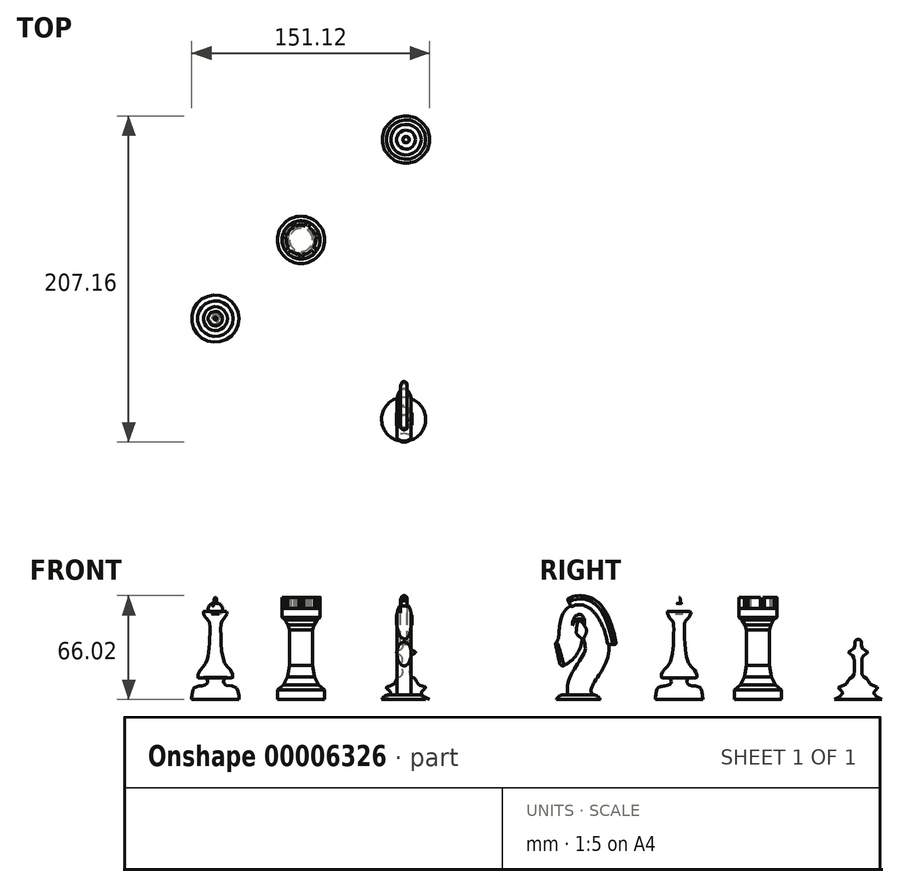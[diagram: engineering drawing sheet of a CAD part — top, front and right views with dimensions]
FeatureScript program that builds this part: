
annotation { "Feature Type Name" : "Feature", "Feature Type Description" : "" }
export const myFeature = defineFeature(function(context is Context, id is Id, definition is map)
    precondition{}
    {
        {
            var Q0;
            Q0=qCreatedBy(makeId("Front.planeOp"),FACE);
            var sketch = newSketch(context, id + "F0", { "sketchPlane" : qUnion([Q0])});
            skLineSegment(sketch, "E0", {"start": v(-54.42, 8.51) * mm, "end": v(-39.42, 8.51) * mm});
            skLineSegment(sketch, "E1", {"start": v(-54.42, 8.51) * mm, "end": v(-54.42, 73.51) * mm});
            skPoint(sketch, "E2.1.internal.orphan", {"position": v(-39.42, 9.76) * mm});
            skPoint(sketch, "E3.1.internal.orphan", {"position": v(-52.69, 73.51) * mm});
            skFitSpline(sketch, "E4", {"points": [v(-54.42, 73.51) * mm, v(-53.55, 72.1) * mm, v(-53.46, 69.73) * mm, v(-52.69, 69.64) * mm, v(-50.55, 68.18) * mm, v(-50.2, 65.25) * mm, v(-52.02, 62.88) * mm, v(-47.1, 64.52) * mm, v(-48.6, 60.17) * mm, v(-50.48, 58.23) * mm, v(-50.97, 52.34) * mm, v(-50.18, 38.13) * mm, v(-47.52, 30.23) * mm, v(-44.3, 26.7) * mm, v(-43.47, 22.32) * mm, v(-47.93, 22.35) * mm, v(-49, 18.48) * mm, v(-41.7, 16.43) * mm, v(-39.8, 12.66) * mm, v(-39.42, 8.51) * mm], "startDerivative": vector(29.5, -28.55) * mm, "endDerivative": vector(-7.12, -67.96) * mm});
            skSolve(sketch);
        }
        {
            var Q0;
            Q0=makeQuery(id+"F0.imprint","IMPRINT",FACE,{"disambiguationData":[TD([[makeQuery(id+"F0.imprint","IMPRINT",EDGE,{"derivedFrom":sQuery(id+"F0.wireOp",EDGE,"E0")}),1.0]])]});
            var Q1;
            Q1=sQuery(id+"F0.wireOp",EDGE,"E1");
            revolve(context, id + "F1", {"entities" : qUnion([Q0]), "axis" : qUnion([Q1]), "revolveType" : RevolveType.FULL});
        }
        {
            var Q0;
            Q0=qCreatedBy(makeId("Top.planeOp"),FACE);
            var sketch = newSketch(context, id + "F2", { "sketchPlane" : qUnion([Q0])});
            skCircle(sketch, "E5", {"center": v(65.14, -64.02) * mm, "radius": 14 * mm});
            skSolve(sketch);
        }
        {
            var Q0;
            Q0=makeQuery(id+"F2.imprint","IMPRINT",FACE,{"disambiguationData":[TD([[makeQuery(id+"F2.imprint","IMPRINT",EDGE,{"derivedFrom":sQuery(id+"F2.wireOp",EDGE,"E5")}),1.0]])]});
            extrude(context, id + "F3", {"entities" : qUnion([Q0]), "depth" : 3 * mm});
        }
        {
            var Q0;
            Q0=makeQuery(id+"F3.opExtrude","CAP_EDGE",EDGE,{"disambiguationData":[OSD([sQuery(id+"F2.wireOp",EDGE,"E5")])],"isStart":false});
            fillet(context, id + "F4", {"entities" : qUnion([Q0]), "radius" : 5 * mm, "tangentPropagation" : true, "allowEdgeOverflow" : false});
        }
        {
            var Q0;
            Q0=makeQuery(id+"F3.opExtrude","CAP_FACE",FACE,{"disambiguationData":[OSD([sQuery(id+"F2.wireOp",EDGE,"E5")])],"isStart":false});
            var sketch = newSketch(context, id + "F5", { "sketchPlane" : qUnion([Q0])});
            skLineSegment(sketch, "E6", {"start": v(65.48, -63.98) * mm, "end": v(65.48, -61.79) * mm, "construction": true});
            skPoint(sketch, "E7", {"position": v(65.48, -62.88) * mm});
            skEllipse(sketch, "E8", {"center": v(65.48, -62.88) * mm, "majorRadius": 7.78 * mm, "minorRadius": 4.5 * mm, "majorAxis": v(-0.01, 1)});
            skSolve(sketch);
        }
        {
            var Q0;
            Q0=sQuery(id+"F5.wireOp",EDGE,"E6");
            var Q1;
            Q1=sQuery(id+"F5.wireOp",EDGE,"7c3d4466-9b8f-44b1-8b03-aff673ece0ba.0");
            cPlane(context, id + "F6", {"entities" : qUnion([Q0, Q1]), "cplaneType" : CPlaneType.LINE_ANGLE, "offset" : 5 * mm, "angle" : 90 * degree, "width" : 150 * mm, "height" : 150 * mm});
        }
        {
            var Q0;
            Q0=qCreatedBy(id+"F6.planeOp",FACE);
            var sketch = newSketch(context, id + "F7", { "sketchPlane" : qUnion([Q0])});
            skLineSegment(sketch, "E9.0", {"start": v(-63.98, 3) * mm, "end": v(-61.79, 3) * mm});
            skPoint(sketch, "E10", {"position": v(-62.88, 3) * mm});
            skLineSegment(sketch, "E11", {"start": v(-61.79, 3) * mm, "end": v(-61.79, 53) * mm, "construction": true});
            skFitSpline(sketch, "E12", {"points": [v(-62.88, 3) * mm, v(-62.88, 9.44) * mm, v(-57.92, 18.86) * mm, v(-52.19, 33.4) * mm, v(-61.79, 53) * mm, v(-66.92, 50.95) * mm, v(-68.93, 40.26) * mm, v(-77.02, 28.25) * mm], "startDerivative": vector(-13.9, 64.01) * mm, "endDerivative": vector(-112.3, -51.14) * mm});
            skSolve(sketch);
        }
        {
            var Q0;
            Q0=makeQuery(id+"F5.imprint","IMPRINT",FACE,{"disambiguationData":[TD([[makeQuery(id+"F5.imprint","IMPRINT",EDGE,{"derivedFrom":sQuery(id+"F5.wireOp",EDGE,"E8")}),1.0]])]});
            var Q1;
            Q1=sQuery(id+"F7.wireOp",EDGE,"E12");
            sweep(context, id + "F8", {"operationType" : NewBodyOperationType.ADD, "profiles" : qUnion([Q0]), "path" : qUnion([Q1])});
        }
        {
            var Q0;
            Q0=qCreatedBy(id+"F6.planeOp",FACE);
            cPlane(context, id + "F9", {"entities" : qUnion([Q0]), "cplaneType" : CPlaneType.OFFSET, "offset" : 25 * mm, "width" : 150 * mm, "height" : 150 * mm});
        }
        {
            var Q0;
            Q0=qCreatedBy(id+"F9.planeOp",FACE);
            var sketch = newSketch(context, id + "F10", { "sketchPlane" : qUnion([Q0])});
            skFitSpline(sketch, "E13.0", {"points": [v(-62.37, 3) * mm, v(-62.85, 5.23) * mm, v(-64.4, 10.59) * mm, v(-50.33, 16.4) * mm, v(-51.17, 32.87) * mm, v(-58.28, 56.27) * mm, v(-68.89, 51.46) * mm, v(-68.1, 39.65) * mm, v(-71.15, 30.92) * mm, v(-77.02, 28.25) * mm]});
            skCircle(sketch, "E14", {"center": v(-63.7, 48.76) * mm, "radius": 10.57 * mm});
            skSolve(sketch);
        }
        {
            var Q0;
            {var subQ0=sQuery(id+"F10.wireOp",EDGE,"E14");var subQ1=sQuery(id+"F10.wireOp",EDGE,"E13.0");var subQ3=makeQuery(id+"F10.imprint","INTERSECT",VERTEX,{"disambiguationData":[OD(0.0)],"derivedFrom":[subQ1,subQ0]});Q0=makeQuery(id+"F10.imprint","IMPRINT",FACE,{"disambiguationData":[TD([[makeQuery(id+"F10.imprint","IMPRINT",EDGE,{"disambiguationData":[TD([[subQ3,1.0]])],"derivedFrom":subQ1}),-1.0]])]});}
            var Q1;
            {var subQ0=sQuery(id+"F10.wireOp",EDGE,"E14");var subQ1=sQuery(id+"F10.wireOp",EDGE,"E13.0");var subQ3=makeQuery(id+"F10.imprint","INTERSECT",VERTEX,{"disambiguationData":[OD(0.0)],"derivedFrom":[subQ1,subQ0]});Q1=makeQuery(id+"F10.imprint","IMPRINT",FACE,{"disambiguationData":[TD([[makeQuery(id+"F10.imprint","IMPRINT",EDGE,{"disambiguationData":[TD([[subQ3,1.0]])],"derivedFrom":subQ1}),1.0]])]});}
            extrude(context, id + "F11", {"entities" : qUnion([Q0, Q1]), "depth" : 8.2 * mm});
        }
        {
            var Q0;
            Q0=qCreatedBy(makeId("Top.planeOp"),FACE);
            var sketch = newSketch(context, id + "F12", { "sketchPlane" : qUnion([Q0])});
            skFitSpline(sketch, "E15.0", {"points": [v(64.78, -54.59) * mm, v(1000, 55.78) * mm, v(-54.68, 333.33) * mm, v(55.94, -70.24) * mm, v(333.33, 64.94) * mm, v(-70.15, 1000) * mm, v(73.94, -70.06) * mm, v(64.78, -54.59) * mm]});
            skLineSegment(sketch, "E16.0", {"start": v(98.68, -53.13) * mm, "end": v(98.68, -74.28) * mm});
            skLineSegment(sketch, "E17", {"start": v(98.68, -63.7) * mm, "end": v(94.58, -63.7) * mm, "construction": true});
            skPoint(sketch, "E18.orphan", {"position": v(90.48, -74.28) * mm});
            skPoint(sketch, "E19.0.start.orphan", {"position": v(90.48, -53.13) * mm});
            skPoint(sketch, "E20", {"position": v(94.58, -63.7) * mm});
            skPoint(sketch, "E21.orphan", {"position": v(90.48, -63.7) * mm});
            skLineSegment(sketch, "E22", {"start": v(61, -62.21) * mm, "end": v(65.48, -62.21) * mm, "construction": true});
            skPoint(sketch, "E23", {"position": v(65.48, -62.21) * mm});
            skPoint(sketch, "E24.orphan", {"position": v(69.96, -62.21) * mm});
            skLineSegment(sketch, "E25", {"start": v(65.48, -62.21) * mm, "end": v(94.58, -62.21) * mm});
            skLineSegment(sketch, "E26", {"start": v(65.48, -62.21) * mm, "end": v(65.48, -55.1) * mm});
            skSolve(sketch);
        }
        {
            var Q0;
            Q0=makeQuery(id+"F11.opExtrude","CAP_EDGE",EDGE,{"disambiguationData":[OSD([sQuery(id+"F10.wireOp",EDGE,"E14")])],"isStart":true});
            fillet(context, id + "F13", {"entities" : qUnion([Q0]), "radius" : 5 * mm, "tangentPropagation" : true, "allowEdgeOverflow" : false});
        }
        {
            var Q0;
            Q0=makeQuery(id+"F11.opExtrude","SWEPT_FACE",FACE,{"disambiguationData":[OSD([sQuery(id+"F10.wireOp",EDGE,"E14")])]});
            var Q1;
            Q1=makeQuery(id+"F11.opExtrude","CAP_EDGE",EDGE,{"disambiguationData":[OSD([sQuery(id+"F10.wireOp",EDGE,"E14")])],"isStart":false});
            fillet(context, id + "F14", {"entities" : qUnion([Q0, Q1]), "radius" : 5 * mm, "tangentPropagation" : true, "allowEdgeOverflow" : false});
        }
        {
            var Q0;
            Q0=makeQuery(id+"F11.opExtrude","SWEPT_BODY",BODY,{"disambiguationData":[OSD([sQuery(id+"F10.wireOp",EDGE,"E14")])]});
            var Q1;
            Q1=sQuery(id+"F12.wireOp",EDGE,"E25");
            transform(context, id + "F15", {"entities" : qUnion([Q0]), "transformType" : TransformType.TRANSLATION_ENTITY, "oppositeDirectionEntity" : true, "transformLine" : qUnion([Q1]), "makeCopy" : false});
        }
        {
            var Q0;
            Q0=qCreatedBy(makeId("Front.planeOp"),FACE);
            cPlane(context, id + "F16", {"entities" : qUnion([Q0]), "cplaneType" : CPlaneType.OFFSET, "offset" : 60 * mm, "width" : 150 * mm, "height" : 150 * mm});
        }
        {
            var Q0;
            Q0=qCreatedBy(id+"F16.planeOp",FACE);
            var sketch = newSketch(context, id + "F17", { "sketchPlane" : qUnion([Q0])});
            skLineSegment(sketch, "E27", {"start": v(68.51, 50.81) * mm, "end": v(68.51, 47.26) * mm});
            skLineSegment(sketch, "E28", {"start": v(62.54, 50.81) * mm, "end": v(62.54, 47.26) * mm});
            skArc(sketch, "E29", {"start": v(62.54, 50.81) * mm, "mid": v(60.5, 49.03) * mm, "end": v(62.54, 47.26) * mm});
            skArc(sketch, "E30", {"start": v(68.51, 47.26) * mm, "mid": v(70.56, 49.03) * mm, "end": v(68.51, 50.81) * mm});
            skLineSegment(sketch, "E31", {"start": v(68.51, 50.81) * mm, "end": v(62.54, 50.81) * mm, "construction": true});
            skSolve(sketch);
        }
        {
            var Q0;
            Q0=qCreatedBy(id+"F6.planeOp",FACE);
            var sketch = newSketch(context, id + "F18", { "sketchPlane" : qUnion([Q0])});
            skFitSpline(sketch, "E32", {"points": [v(-60.02, 49.4) * mm, v(-61.51, 52.33) * mm, v(-63.91, 53.04) * mm, v(-66.19, 51.57) * mm, v(-67.65, 48.67) * mm], "startDerivative": vector(-4.28, 12.7) * mm, "endDerivative": vector(-4.6, -11.84) * mm});
            skSolve(sketch);
        }
        {
            var Q0;
            Q0=makeQuery(id+"F17.imprint","IMPRINT",FACE,{"disambiguationData":[TD([[makeQuery(id+"F17.imprint","IMPRINT",EDGE,{"derivedFrom":sQuery(id+"F17.wireOp",EDGE,"E27")}),1.0]])]});
            var Q1;
            Q1=makeQuery(id+"F17.imprint","IMPRINT",FACE,{"disambiguationData":[TD([[makeQuery(id+"F17.imprint","IMPRINT",EDGE,{"derivedFrom":sQuery(id+"F17.wireOp",EDGE,"E28")}),-1.0]])]});
            var Q2;
            Q2=sQuery(id+"F18.wireOp",EDGE,"E32");
            sweep(context, id + "F19", {"operationType" : NewBodyOperationType.ADD, "profiles" : qUnion([Q0, Q1]), "path" : qUnion([Q2]), "keepProfileOrientation" : true});
        }
        {
            var Q0;
            Q0=qCreatedBy(makeId("Top.planeOp"),FACE);
            cPlane(context, id + "F20", {"entities" : qUnion([Q0]), "cplaneType" : CPlaneType.OFFSET, "offset" : 35 * mm, "width" : 150 * mm, "height" : 150 * mm});
        }
        {
            var Q0;
            Q0=qCreatedBy(id+"F20.planeOp",FACE);
            var sketch = newSketch(context, id + "F21", { "sketchPlane" : qUnion([Q0])});
            skLineSegment(sketch, "E33.top", {"start": v(63.3, -46.58) * mm, "end": v(67.46, -46.58) * mm});
            skLineSegment(sketch, "E33.left", {"start": v(63.3, -42.04) * mm, "end": v(63.3, -46.58) * mm});
            skLineSegment(sketch, "E33.right", {"start": v(67.46, -42.04) * mm, "end": v(67.46, -46.58) * mm});
            skFitSpline(sketch, "E34", {"points": [v(67.46, -42.04) * mm, v(66.8, -40.41) * mm, v(65.17, -39.87) * mm, v(63.97, -40.6) * mm, v(63.3, -42.04) * mm], "startDerivative": vector(-1.48, 7.01) * mm, "endDerivative": vector(-2.13, -6.29) * mm});
            skSolve(sketch);
        }
        {
            var Q0;
            Q0=qCreatedBy(id+"F6.planeOp",FACE);
            var sketch = newSketch(context, id + "F22", { "sketchPlane" : qUnion([Q0])});
            skFitSpline(sketch, "E35.0", {"points": [v(-62.37, 3) * mm, v(-62.85, 5.23) * mm, v(-64.4, 10.59) * mm, v(-50.34, 16.4) * mm, v(-51.16, 32.87) * mm, v(-58.33, 56.26) * mm, v(-68.88, 51.45) * mm, v(-68.1, 39.65) * mm, v(-71.15, 30.92) * mm, v(-77.02, 28.25) * mm]});
            skPoint(sketch, "E36", {"position": v(-65.58, 52.52) * mm});
            skPoint(sketch, "E37", {"position": v(-52.3, 34.86) * mm});
            skPoint(sketch, "E38.orphan", {"position": v(-62.88, 3) * mm});
            skPoint(sketch, "E39.orphan", {"position": v(-77.02, 28.25) * mm});
            skFitSpline(sketch, "E40.0", {"points": [v(-44.9, 36.47) * mm, v(-45.2, 37.92) * mm, v(-45.91, 40.92) * mm, v(-47.02, 44.7) * mm, v(-48.07, 47.64) * mm, v(-48.94, 49.8) * mm, v(-49.93, 51.9) * mm, v(-51.07, 53.93) * mm, v(-52.2, 55.57) * mm, v(-53.27, 56.85) * mm, v(-54.19, 57.78) * mm, v(-55.24, 58.69) * mm, v(-56.26, 59.39) * mm, v(-57.18, 59.9) * mm, v(-58.15, 60.36) * mm, v(-59.4, 60.8) * mm, v(-60.95, 61.12) * mm, v(-62.47, 61.24) * mm, v(-63.95, 61.16) * mm, v(-65.83, 60.83) * mm, v(-67.97, 60.06) * mm, v(-69.44, 59.17) * mm, v(-70.12, 58.67) * mm]});
            skSolve(sketch);
        }
        {
            var Q0;
            Q0=makeQuery(id+"F21.imprint","IMPRINT",FACE,{"disambiguationData":[TD([[makeQuery(id+"F21.imprint","IMPRINT",EDGE,{"derivedFrom":sQuery(id+"F21.wireOp",EDGE,"E33.top")}),1.0]])]});
            var Q1;
            Q1=sQuery(id+"F22.wireOp",EDGE,"E40.0");
            sweep(context, id + "F23", {"operationType" : NewBodyOperationType.ADD, "profiles" : qUnion([Q0]), "path" : qUnion([Q1])});
        }
        {
            var Q0;
            Q0=makeQuery(id+"F23.opSweep","CAP_EDGE",EDGE,{"disambiguationData":[OSD([sQuery(id+"F21.wireOp",EDGE,"E33.right"),sQuery(id+"F22.wireOp",VERTEX,"E40.0.start")])],"isStart":true});
            var Q1;
            Q1=makeQuery(id+"F23.opSweep","CAP_EDGE",EDGE,{"disambiguationData":[OSD([sQuery(id+"F21.wireOp",EDGE,"E34"),sQuery(id+"F22.wireOp",VERTEX,"E40.0.start")])],"isStart":true});
            var Q2;
            Q2=makeQuery(id+"F23.opSweep","CAP_EDGE",EDGE,{"disambiguationData":[OSD([sQuery(id+"F21.wireOp",EDGE,"E33.left"),sQuery(id+"F22.wireOp",VERTEX,"E40.0.start")])],"isStart":true});
            var Q3;
            Q3=makeQuery(id+"F23.opSweep","CAP_EDGE",EDGE,{"disambiguationData":[OSD([sQuery(id+"F21.wireOp",EDGE,"E34"),sQuery(id+"F22.wireOp",VERTEX,"E40.0.end")])],"isStart":false});
            var Q4;
            Q4=makeQuery(id+"F23.opSweep","CAP_EDGE",EDGE,{"disambiguationData":[OSD([sQuery(id+"F21.wireOp",EDGE,"E33.right"),sQuery(id+"F22.wireOp",VERTEX,"E40.0.end")])],"isStart":false});
            var Q5;
            Q5=makeQuery(id+"F23.opSweep","CAP_EDGE",EDGE,{"disambiguationData":[OSD([sQuery(id+"F21.wireOp",EDGE,"E33.left"),sQuery(id+"F22.wireOp",VERTEX,"E40.0.end")])],"isStart":false});
            fillet(context, id + "F24", {"entities" : qUnion([Q0, Q1, Q2, Q3, Q4, Q5]), "radius" : 1 * mm, "tangentPropagation" : true, "allowEdgeOverflow" : false});
        }
        {
            var Q0;
            Q0=makeQuery(id+"F8.opSweep","CAP_EDGE",EDGE,{"disambiguationData":[OSD([sQuery(id+"F5.wireOp",EDGE,"E8"),sQuery(id+"F7.wireOp",VERTEX,"E12.end")])],"isStart":false});
            fillet(context, id + "F25", {"entities" : qUnion([Q0]), "radius" : 2 * mm, "tangentPropagation" : true, "allowEdgeOverflow" : false});
        }
        {
            var Q0;
            Q0=qCreatedBy(makeId("Top.planeOp"),FACE);
            cPlane(context, id + "F26", {"entities" : qUnion([Q0]), "cplaneType" : CPlaneType.OFFSET, "offset" : 5 * mm, "width" : 150 * mm, "height" : 150 * mm});
        }
        {
            var Q0;
            Q0=qCreatedBy(id+"F26.planeOp",FACE);
            cPlane(context, id + "F27", {"entities" : qUnion([Q0]), "cplaneType" : CPlaneType.OFFSET, "offset" : 2.5 * mm, "width" : 150 * mm, "height" : 150 * mm});
        }
        {
            var Q0;
            Q0=qCreatedBy(id+"F27.planeOp",FACE);
            cPlane(context, id + "F28", {"entities" : qUnion([Q0]), "cplaneType" : CPlaneType.OFFSET, "offset" : 2.5 * mm, "width" : 150 * mm, "height" : 150 * mm});
        }
        {
            var Q0;
            Q0=qCreatedBy(id+"F28.planeOp",FACE);
            cPlane(context, id + "F29", {"entities" : qUnion([Q0]), "cplaneType" : CPlaneType.OFFSET, "offset" : 2.55 * mm, "width" : 150 * mm, "height" : 150 * mm});
        }
        {
            var Q0;
            Q0=qCreatedBy(id+"F29.planeOp",FACE);
            cPlane(context, id + "F30", {"entities" : qUnion([Q0]), "cplaneType" : CPlaneType.OFFSET, "offset" : 2.5 * mm, "width" : 150 * mm, "height" : 150 * mm});
        }
        {
            var Q0;
            Q0=qCreatedBy(id+"F30.planeOp",FACE);
            cPlane(context, id + "F31", {"entities" : qUnion([Q0]), "cplaneType" : CPlaneType.OFFSET, "offset" : 5 * mm, "width" : 150 * mm, "height" : 150 * mm});
        }
        {
            var Q0;
            Q0=qCreatedBy(id+"F31.planeOp",FACE);
            cPlane(context, id + "F32", {"entities" : qUnion([Q0]), "cplaneType" : CPlaneType.OFFSET, "offset" : 2.5 * mm, "width" : 150 * mm, "height" : 150 * mm});
        }
        {
            var Q0;
            Q0=qCreatedBy(id+"F32.planeOp",FACE);
            cPlane(context, id + "F33", {"entities" : qUnion([Q0]), "cplaneType" : CPlaneType.OFFSET, "offset" : 2.5 * mm, "width" : 150 * mm, "height" : 150 * mm});
        }
        {
            var Q0;
            Q0=qCreatedBy(id+"F33.planeOp",FACE);
            cPlane(context, id + "F34", {"entities" : qUnion([Q0]), "cplaneType" : CPlaneType.OFFSET, "offset" : 2.5 * mm, "width" : 150 * mm, "height" : 150 * mm});
        }
        {
            var Q0;
            Q0=qCreatedBy(id+"F34.planeOp",FACE);
            cPlane(context, id + "F35", {"entities" : qUnion([Q0]), "cplaneType" : CPlaneType.OFFSET, "offset" : 2.5 * mm, "width" : 150 * mm, "height" : 150 * mm});
        }
        {
            var Q0;
            Q0=qCreatedBy(makeId("Top.planeOp"),FACE);
            var sketch = newSketch(context, id + "F36", { "sketchPlane" : qUnion([Q0])});
            skCircle(sketch, "E41", {"center": v(66.67, 113.7) * mm, "radius": 15 * mm});
            skSolve(sketch);
        }
        {
            var Q0;
            Q0=qCreatedBy(id+"F26.planeOp",FACE);
            var sketch = newSketch(context, id + "F37", { "sketchPlane" : qUnion([Q0])});
            skPoint(sketch, "E42.0", {"position": v(66.67, 113.7) * mm});
            skCircle(sketch, "E43", {"center": v(66.67, 113.7) * mm, "radius": 10 * mm});
            skSolve(sketch);
        }
        {
            var Q0;
            Q0=qCreatedBy(id+"F27.planeOp",FACE);
            var sketch = newSketch(context, id + "F38", { "sketchPlane" : qUnion([Q0])});
            skPoint(sketch, "E44.0", {"position": v(66.67, 113.7) * mm});
            skCircle(sketch, "E45", {"center": v(66.67, 113.7) * mm, "radius": 12.5 * mm});
            skSolve(sketch);
        }
        {
            var Q0;
            Q0=qCreatedBy(id+"F28.planeOp",FACE);
            var sketch = newSketch(context, id + "F39", { "sketchPlane" : qUnion([Q0])});
            skPoint(sketch, "E46.0", {"position": v(66.67, 113.7) * mm});
            skCircle(sketch, "E47", {"center": v(66.67, 113.7) * mm, "radius": 7.5 * mm});
            skSolve(sketch);
        }
        {
            var Q0;
            Q0=qCreatedBy(id+"F29.planeOp",FACE);
            var sketch = newSketch(context, id + "F40", { "sketchPlane" : qUnion([Q0])});
            skPoint(sketch, "E48.0", {"position": v(66.67, 113.7) * mm});
            skCircle(sketch, "E49", {"center": v(66.67, 113.7) * mm, "radius": 6.25 * mm});
            skSolve(sketch);
        }
        {
            var Q0;
            Q0=qCreatedBy(id+"F30.planeOp",FACE);
            var sketch = newSketch(context, id + "F41", { "sketchPlane" : qUnion([Q0])});
            skPoint(sketch, "E50.0", {"position": v(66.67, 113.7) * mm});
            skCircle(sketch, "E51", {"center": v(66.67, 113.7) * mm, "radius": 3 * mm});
            skSolve(sketch);
        }
        {
            var Q0;
            Q0=qCreatedBy(id+"F31.planeOp",FACE);
            var sketch = newSketch(context, id + "F42", { "sketchPlane" : qUnion([Q0])});
            skPoint(sketch, "E52.0", {"position": v(66.67, 113.7) * mm});
            skCircle(sketch, "E53", {"center": v(66.67, 113.7) * mm, "radius": 2.5 * mm});
            skSolve(sketch);
        }
        {
            var Q0;
            Q0=qCreatedBy(id+"F32.planeOp",FACE);
            var sketch = newSketch(context, id + "F43", { "sketchPlane" : qUnion([Q0])});
            skCircle(sketch, "E54.0", {"center": v(66.67, 113.7) * mm, "radius": 2.5 * mm});
            skSolve(sketch);
        }
        {
            var Q0;
            Q0=qCreatedBy(id+"F33.planeOp",FACE);
            var sketch = newSketch(context, id + "F44", { "sketchPlane" : qUnion([Q0])});
            skCircle(sketch, "E55.0", {"center": v(66.67, 113.7) * mm, "radius": 2.5 * mm});
            skSolve(sketch);
        }
        {
            var Q0;
            Q0=qCreatedBy(id+"F34.planeOp",FACE);
            var sketch = newSketch(context, id + "F45", { "sketchPlane" : qUnion([Q0])});
            skPoint(sketch, "E56.0", {"position": v(66.67, 113.7) * mm});
            skCircle(sketch, "E57", {"center": v(66.67, 113.7) * mm, "radius": 3 * mm});
            skSolve(sketch);
        }
        {
            var Q0;
            Q0=qCreatedBy(id+"F35.planeOp",FACE);
            var sketch = newSketch(context, id + "F46", { "sketchPlane" : qUnion([Q0])});
            skPoint(sketch, "E58.0", {"position": v(66.67, 113.7) * mm});
            skCircle(sketch, "E59", {"center": v(66.67, 113.7) * mm, "radius": 6 * mm});
            skSolve(sketch);
        }
        {
            var Q0;
            Q0=qCreatedBy(id+"F35.planeOp",FACE);
            cPlane(context, id + "F47", {"entities" : qUnion([Q0]), "cplaneType" : CPlaneType.OFFSET, "offset" : 2 * mm, "width" : 150 * mm, "height" : 150 * mm});
        }
        {
            var Q0;
            Q0=qCreatedBy(id+"F47.planeOp",FACE);
            cPlane(context, id + "F48", {"entities" : qUnion([Q0]), "cplaneType" : CPlaneType.OFFSET, "offset" : 3 * mm, "width" : 150 * mm, "height" : 150 * mm});
        }
        {
            var Q0;
            Q0=qCreatedBy(id+"F48.planeOp",FACE);
            cPlane(context, id + "F49", {"entities" : qUnion([Q0]), "cplaneType" : CPlaneType.OFFSET, "offset" : 3 * mm, "width" : 150 * mm, "height" : 150 * mm});
        }
        {
            var Q0;
            Q0=qCreatedBy(id+"F47.planeOp",FACE);
            var sketch = newSketch(context, id + "F50", { "sketchPlane" : qUnion([Q0])});
            skPoint(sketch, "E60.0", {"position": v(66.67, 113.7) * mm});
            skCircle(sketch, "E61", {"center": v(66.67, 113.7) * mm, "radius": 3 * mm});
            skSolve(sketch);
        }
        {
            var Q0;
            Q0=qCreatedBy(id+"F48.planeOp",FACE);
            var sketch = newSketch(context, id + "F51", { "sketchPlane" : qUnion([Q0])});
            skPoint(sketch, "E62.0", {"position": v(66.67, 113.7) * mm});
            skCircle(sketch, "E63", {"center": v(66.67, 113.7) * mm, "radius": 2 * mm});
            skSolve(sketch);
        }
        {
            var Q0;
            Q0=qCreatedBy(id+"F49.planeOp",FACE);
            var sketch = newSketch(context, id + "F52", { "sketchPlane" : qUnion([Q0])});
            skCircle(sketch, "E64.0", {"center": v(66.67, 113.7) * mm, "radius": 2 * mm});
            skSolve(sketch);
        }
        {
            var Q0;
            Q0=makeQuery(id+"F36.imprint","IMPRINT",FACE,{"disambiguationData":[TD([[makeQuery(id+"F36.imprint","IMPRINT",EDGE,{"derivedFrom":sQuery(id+"F36.wireOp",EDGE,"E41")}),1.0]])]});
            var Q1;
            Q1=makeQuery(id+"F37.imprint","IMPRINT",FACE,{"disambiguationData":[TD([[makeQuery(id+"F37.imprint","IMPRINT",EDGE,{"derivedFrom":sQuery(id+"F37.wireOp",EDGE,"E43")}),1.0]])]});
            var Q2;
            Q2=makeQuery(id+"F38.imprint","IMPRINT",FACE,{"disambiguationData":[TD([[makeQuery(id+"F38.imprint","IMPRINT",EDGE,{"derivedFrom":sQuery(id+"F38.wireOp",EDGE,"E45")}),1.0]])]});
            var Q3;
            Q3=makeQuery(id+"F39.imprint","IMPRINT",FACE,{"disambiguationData":[TD([[makeQuery(id+"F39.imprint","IMPRINT",EDGE,{"derivedFrom":sQuery(id+"F39.wireOp",EDGE,"E47")}),1.0]])]});
            var Q4;
            Q4=makeQuery(id+"F40.imprint","IMPRINT",FACE,{"disambiguationData":[TD([[makeQuery(id+"F40.imprint","IMPRINT",EDGE,{"derivedFrom":sQuery(id+"F40.wireOp",EDGE,"E49")}),1.0]])]});
            var Q5;
            Q5=makeQuery(id+"F41.imprint","IMPRINT",FACE,{"disambiguationData":[TD([[makeQuery(id+"F41.imprint","IMPRINT",EDGE,{"derivedFrom":sQuery(id+"F41.wireOp",EDGE,"E51")}),1.0]])]});
            var Q6;
            Q6=makeQuery(id+"F42.imprint","IMPRINT",FACE,{"disambiguationData":[TD([[makeQuery(id+"F42.imprint","IMPRINT",EDGE,{"derivedFrom":sQuery(id+"F42.wireOp",EDGE,"E53")}),1.0]])]});
            var Q7;
            Q7=makeQuery(id+"F43.imprint","IMPRINT",FACE,{"disambiguationData":[TD([[makeQuery(id+"F43.imprint","IMPRINT",EDGE,{"derivedFrom":sQuery(id+"F43.wireOp",EDGE,"E54.0")}),1.0]])]});
            var Q8;
            Q8=makeQuery(id+"F44.imprint","IMPRINT",FACE,{"disambiguationData":[TD([[makeQuery(id+"F44.imprint","IMPRINT",EDGE,{"derivedFrom":sQuery(id+"F44.wireOp",EDGE,"E55.0")}),1.0]])]});
            var Q9;
            Q9=makeQuery(id+"F45.imprint","IMPRINT",FACE,{"disambiguationData":[TD([[makeQuery(id+"F45.imprint","IMPRINT",EDGE,{"derivedFrom":sQuery(id+"F45.wireOp",EDGE,"E57")}),1.0]])]});
            var Q10;
            Q10=makeQuery(id+"F46.imprint","IMPRINT",FACE,{"disambiguationData":[TD([[makeQuery(id+"F46.imprint","IMPRINT",EDGE,{"derivedFrom":sQuery(id+"F46.wireOp",EDGE,"E59")}),1.0]])]});
            var Q11;
            Q11=makeQuery(id+"F50.imprint","IMPRINT",FACE,{"disambiguationData":[TD([[makeQuery(id+"F50.imprint","IMPRINT",EDGE,{"derivedFrom":sQuery(id+"F50.wireOp",EDGE,"E61")}),1.0]])]});
            var Q12;
            Q12=makeQuery(id+"F51.imprint","IMPRINT",FACE,{"disambiguationData":[TD([[makeQuery(id+"F51.imprint","IMPRINT",EDGE,{"derivedFrom":sQuery(id+"F51.wireOp",EDGE,"E63")}),1.0]])]});
            var Q13;
            Q13=makeQuery(id+"F52.imprint","IMPRINT",FACE,{"disambiguationData":[TD([[makeQuery(id+"F52.imprint","IMPRINT",EDGE,{"derivedFrom":sQuery(id+"F52.wireOp",EDGE,"E64.0")}),1.0]])]});
            loft(context, id + "F53", {"sheetProfilesArray" : [{ "sheetProfileEntities" : qUnion([Q0]) }, { "sheetProfileEntities" : qUnion([Q1]) }, { "sheetProfileEntities" : qUnion([Q2]) }, { "sheetProfileEntities" : qUnion([Q3]) }, { "sheetProfileEntities" : qUnion([Q4]) }, { "sheetProfileEntities" : qUnion([Q5]) }, { "sheetProfileEntities" : qUnion([Q6]) }, { "sheetProfileEntities" : qUnion([Q7]) }, { "sheetProfileEntities" : qUnion([Q8]) }, { "sheetProfileEntities" : qUnion([Q9]) }, { "sheetProfileEntities" : qUnion([Q10]) }, { "sheetProfileEntities" : qUnion([Q11]) }, { "sheetProfileEntities" : qUnion([Q12]) }, { "sheetProfileEntities" : qUnion([Q13]) }]});
        }
        {
            var Q0;
            Q0=makeQuery(id+"F53.opLoft","MID_CAP_EDGE",EDGE,{"disambiguationData":[OSD([sQuery(id+"F36.wireOp",EDGE,"E41"),sQuery(id+"F52.wireOp",EDGE,"E64.0")])],"capPos":13.0});
            fillet(context, id + "F54", {"entities" : qUnion([Q0]), "radius" : 1.5 * mm, "tangentPropagation" : true, "allowEdgeOverflow" : false});
        }
        {
            var Q0;
            Q0=qCreatedBy(makeId("Right.planeOp"),FACE);
            var sketch = newSketch(context, id + "F55", { "sketchPlane" : qUnion([Q0])});
            skLineSegment(sketch, "E65.0", {"start": v(15, 8.51) * mm, "end": v(-15, 8.51) * mm});
            skLineSegment(sketch, "E66.0", {"start": v(-78.02, 0) * mm, "end": v(-50.02, 0) * mm});
            skLineSegment(sketch, "E67", {"start": v(-50.02, 0) * mm, "end": v(2.9, 0) * mm});
            skLineSegment(sketch, "E68", {"start": v(2.9, 0) * mm, "end": v(2.9, 8.51) * mm});
            skSolve(sketch);
        }
        {
            var Q0;
            Q0=makeQuery(id+"F1.opRevolve","SWEPT_BODY",BODY,{"disambiguationData":[OSD([sQuery(id+"F0.wireOp",EDGE,"E0"),sQuery(id+"F0.wireOp",EDGE,"E1"),sQuery(id+"F0.wireOp",EDGE,"E4")])]});
            var Q1;
            Q1=sQuery(id+"F55.wireOp",EDGE,"E68");
            transform(context, id + "F56", {"entities" : qUnion([Q0]), "transformType" : TransformType.TRANSLATION_ENTITY, "oppositeDirectionEntity" : true, "transformLine" : qUnion([Q1]), "makeCopy" : false});
        }
        {
            var Q0;
            Q0=qCreatedBy(makeId("Right.planeOp"),FACE);
            var sketch = newSketch(context, id + "F57", { "sketchPlane" : qUnion([Q0])});
            skLineSegment(sketch, "E69", {"start": v(606.83, 0) * mm, "end": v(606.83, 551.92) * mm});
            skLineSegment(sketch, "E70", {"start": v(50, 0) * mm, "end": v(50, 58) * mm});
            skLineSegment(sketch, "E71", {"start": v(50, 0) * mm, "end": v(35, 0) * mm});
            skLineSegment(sketch, "E72", {"start": v(35, 0) * mm, "end": v(35, 6.13) * mm});
            skLineSegment(sketch, "E73", {"start": v(35, 6.13) * mm, "end": v(38.85, 9.24) * mm});
            skLineSegment(sketch, "E74", {"start": v(38.85, 9.24) * mm, "end": v(41.4, 14.4) * mm});
            skLineSegment(sketch, "E75", {"start": v(41.4, 14.4) * mm, "end": v(42.7, 21.62) * mm});
            skLineSegment(sketch, "E76", {"start": v(42.7, 21.62) * mm, "end": v(42.7, 44.31) * mm});
            skLineSegment(sketch, "E77", {"start": v(42.7, 58) * mm, "end": v(50, 58) * mm});
            skLineSegment(sketch, "E78", {"start": v(42.7, 58) * mm, "end": v(37.9, 58) * mm});
            skLineSegment(sketch, "E79", {"start": v(37.9, 58) * mm, "end": v(37.9, 52.22) * mm});
            skLineSegment(sketch, "E80", {"start": v(37.9, 52.22) * mm, "end": v(39.95, 50.47) * mm});
            skLineSegment(sketch, "E81", {"start": v(39.95, 50.47) * mm, "end": v(41.71, 47.3) * mm});
            skLineSegment(sketch, "E82", {"start": v(41.71, 47.3) * mm, "end": v(42.7, 44.31) * mm});
            skSolve(sketch);
        }
        {
            var Q0;
            Q0=makeQuery(id+"F57.imprint","IMPRINT",FACE,{"disambiguationData":[TD([[makeQuery(id+"F57.imprint","IMPRINT",EDGE,{"derivedFrom":sQuery(id+"F57.wireOp",EDGE,"E70")}),1.0]])]});
            var Q1;
            Q1=sQuery(id+"F57.wireOp",EDGE,"E70");
            revolve(context, id + "F58", {"entities" : qUnion([Q0]), "axis" : qUnion([Q1]), "revolveType" : RevolveType.FULL});
        }
        {
            var Q0;
            Q0=makeQuery(id+"F58.opRevolve","SWEPT_FACE",FACE,{"disambiguationData":[OSD([sQuery(id+"F57.wireOp",EDGE,"E77"),sQuery(id+"F57.wireOp",EDGE,"E78")])]});
            var sketch = newSketch(context, id + "F59", { "sketchPlane" : qUnion([Q0])});
            skLineSegment(sketch, "E83", {"start": v(-6.23, 60.4) * mm, "end": v(-4.67, 57.8) * mm});
            skLineSegment(sketch, "E84", {"start": v(-8.5, 53.2) * mm, "end": v(-11.34, 54.26) * mm});
            skPoint(sketch, "E85", {"position": v(-3.11, 55.2) * mm});
            skPoint(sketch, "E86", {"position": v(-5.67, 52.13) * mm});
            skPoint(sketch, "E87", {"position": v(-8.5, 53.2) * mm});
            skPoint(sketch, "E88", {"position": v(-4.67, 57.8) * mm});
            skArc(sketch, "E89", {"start": v(-4.67, 57.8) * mm, "mid": v(-7.24, 56.04) * mm, "end": v(-8.5, 53.2) * mm});
            skPoint(sketch, "E90.0.center.orphan", {"position": v(0, 50) * mm});
            skArc(sketch, "E91", {"start": v(-6.23, 60.4) * mm, "mid": v(-9.3, 57.76) * mm, "end": v(-11.34, 54.26) * mm});
            skSolve(sketch);
        }
        {
            var Q0;
            Q0=makeQuery(id+"F59.imprint","IMPRINT",FACE,{"disambiguationData":[TD([[makeQuery(id+"F59.imprint","IMPRINT",EDGE,{"derivedFrom":sQuery(id+"F59.wireOp",EDGE,"E83")}),-1.0]])]});
            extrude(context, id + "F60", {"entities" : qUnion([Q0]), "depth" : 7 * mm});
        }
        {
            var Q0;
            Q0=makeQuery(id+"F60.opExtrude","SWEPT_BODY",BODY,{"disambiguationData":[OSD([sQuery(id+"F59.wireOp",EDGE,"E83"),sQuery(id+"F59.wireOp",EDGE,"E84"),sQuery(id+"F59.wireOp",EDGE,"E89"),sQuery(id+"F59.wireOp",EDGE,"E91")])]});
            var Q1;
            Q1=sQuery(id+"F57.wireOp",EDGE,"E70");
            circularPattern(context, id + "F61", {"entities" : qUnion([Q0]), "axis" : qUnion([Q1]), "angle" : 52 * degree, "instanceCount" : 7});
        }
    });
